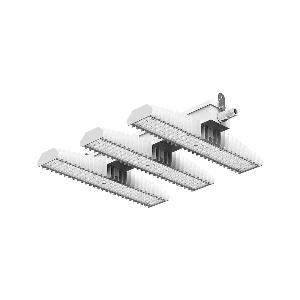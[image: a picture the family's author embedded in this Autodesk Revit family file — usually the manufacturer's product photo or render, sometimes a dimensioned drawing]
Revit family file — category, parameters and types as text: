
# Revit family: 3f_filippi_-_3f_lem_ho_concentrato_3f_filippi_-_58961_-_3f_lem_3_ho_led_210_cr_conc
name_source: partatom
category: Lighting Fixtures
units: mm (PartAtom-declared; Revit-internal decimal feet)

## family parameters
Cut with Voids When Loaded = No
Host = Face
Light Source = No
Part Type = Normal
Room Calculation Point = No
Round Connector Dimension = Use Diameter
Shared = No

## types (1)
- 3F Filippi - 3F LEM HO Concentrato (1 x LED, 32474 lm, 207 W, 4000 K)
    Apparent Load = 207 VA
    Approval mark = CE
    CIE Flux Codes = 83 96 99 100 100
    Color Rendering = 80
    Color Temperature = 4000 K
    Control Gear = Electronic ballast
    Default Elevation = 1800 mm
    Description = Industrial luminaire with high light output and high luminous efficiency designed with the most innovative technologies for environments with temperature up to 55°C.

ILLUMINOTECHNICAL
Luminous efficiency 100% (DLOR 100%, ULOR 0%).
Initial luminous flux of the luminaire 32474 lm.
Direct symmetric narrow distribution: the illuminated area has a elliptical shape.
Installation Interdistance Transv.D = 0.52 x hu - Long.D = 1.16 x hu.
Tabular UGR (CIE 117 - 4H-8H; S=0.25H; 70/50/20): RUG 18.5 - 22.3.
Beam angle: 31° - 73°.
Luminous efficacy 157 lm/W.
Lifetime (L93/B10): 30000 h. (tq+25°C)
Lifetime (L90/B10): 50000 h. (tq+25°C)
Lifetime (L85/B10): 80000 h. (tq+25°C)
Lifetime (L80/B10): 100000 h. (tq+25°C)
Lifetime (L85/B10): 50000 h. (tq+55°C)
Sudden decreased luminous flux after 50000 hours: 0% (C0).
Photobiological safety in compliance with IEC/TR 62778: RG0 risk exempt, (IEC 62471).
In compliance with IEC/EN 62722-2-1 - IEC/EN 62717 standards.

SOURCE
3 Mid-Power linear LED modules 70W/840.
Energy efficiency class (UE 2019/2020 - UE 2019/2015): C.
CIE 13.3 Colour rendering index: CRI >80 (R9 <50%).
IES TM-30 Fidelity Index: Rf = 84 Rg = 95.
CCT nominal colour temperature 4000 K.
Colour initial tolerance (MacAdam): SDCM 3.

MECHANICAL
Passive modular heatsinks in die-casted aluminium, painted in white colour.
To optimize the thermal management of the LED module, the heatsinks are oversized and provided with self-cleaning of cooling fins.
Wiring body in aluminium and galvanised steel anchored solidly to the sinks and thermally separated.
3F Lens lenses with high luminous efficiency, transparent methacrylate (PMMA), fixed to the LED modules.
Fixing brackets in stainless steel.
Luminaire with limited surface temperature. - D - (EN 60598-2-24)
Dimensions: 657x542 mm, height 129 mm. Weight 13.49 kg.
IP65 protection degree.
Mechanical strength to impacts IK06 (1 joule).
Glow-wire test resistance 650°C.

ELECTRICAL
Halogen Free electronic wiring 230V-50/60Hz, power factor 0.97, THD <25%, constant output current, class I, 2 driver.
Power of the luminaire 207 W.
ENEC - CE.
SAFE FLICKER: PstLM=<1 and SVM=<0.4 (IEC TR 61547-1 and IEC TR 63158), to ensure a more comfortable and safe light.
Luminaire compliant with EN 60598-2-22 for power supply from a centralised emergency system CPSS (Central Power Supply System), not incorporated in the luminaire - high risk areas excluded. The default power and flux are 100% in AC and 100% in DC.
Ambient temperature from -30°C to +55°C.
Temperature class T6 max 85°C.
Quick connection via M20 3P connector with 9-13 mm tightening range.
Power unit positioned on a separate compartment by the LED module to ensure optimum temperatures of cabling components, to be inspectable and maintainable.
Relative humidity UR: <85%.

INSTALLATION
Ceiling / Suspended / Wall.
All accessories dedicated to this product are available on the Catalog and on our website www.3F-Filippi.com.

APPLICATIONS
In commercial environments, exhibition and industrial areas, stores, open areas or with shelves.
Environments in which it is necessary a total protection against falling fragments (eg environments with foodstuffs or machines with moving parts or with extreme temperature changes), use luminaires with polycarbonate lenses.

WARNING
Fixture not suitable for cold stores with an ambient temperature <0°C and/or relative humidity >85%.
Luminaire designed for disposal/recycling at end-of-life.
Replaceable (LED only) light source by a professional. Replaceable control gear by a professional.
    Height = 129 mm
    Lamp = 1 x LED
    Lamp Light Flux = 32474 lm
    Lamp Power = 207 W
    Lamp count = 1
    Length = 657 mm
    Lifetime = 50000 h
    Luminous efficacy = 157 lm/W
    Manufacturer = 3F Filippi
    ModVariant = No
    Model = 3F Filippi - 58961 - 3F LEM 3 HO LED 210 CR CONC
    Mounting Place = Ceiling
    Mounting Type = Pendant
    Number of Poles = 1
    OnlyDefault = Yes
    Power Factor = 1
    Product Name = 3F Filippi - 3F LEM HO Concentrato
    Product group = pendant luminaire
    ProductGroupID = 9
    Protection Class = Protection class I
    Protection Degree = IP 65
    RLX_Detail_Level = 1
    RLX_Emergency_Light_Flux = 0 lm
    RLX_Emergency_Type = 0
    RLX_Emergency_Type_DB = No
    RlxData = <blob elided: 100965 chars, md5=5b4d62b1>
    Socket = socket
    Standby Power = 0 W
    System Light Flux = 32474 lm
    System Power = 207 W
    Type Comments = Product without accessories
    Type Image = 3f_filippi_-_lem_3.jpg
    URL = http://relux.com
    VarID = ---
    Voltage = 0 V
    Weight = 0.00 kg
    Width = 542 mm

## geometry (parser evidence)
native form markers: Blend x4, Sweep x10
no freeform markers — native parametric forms only
